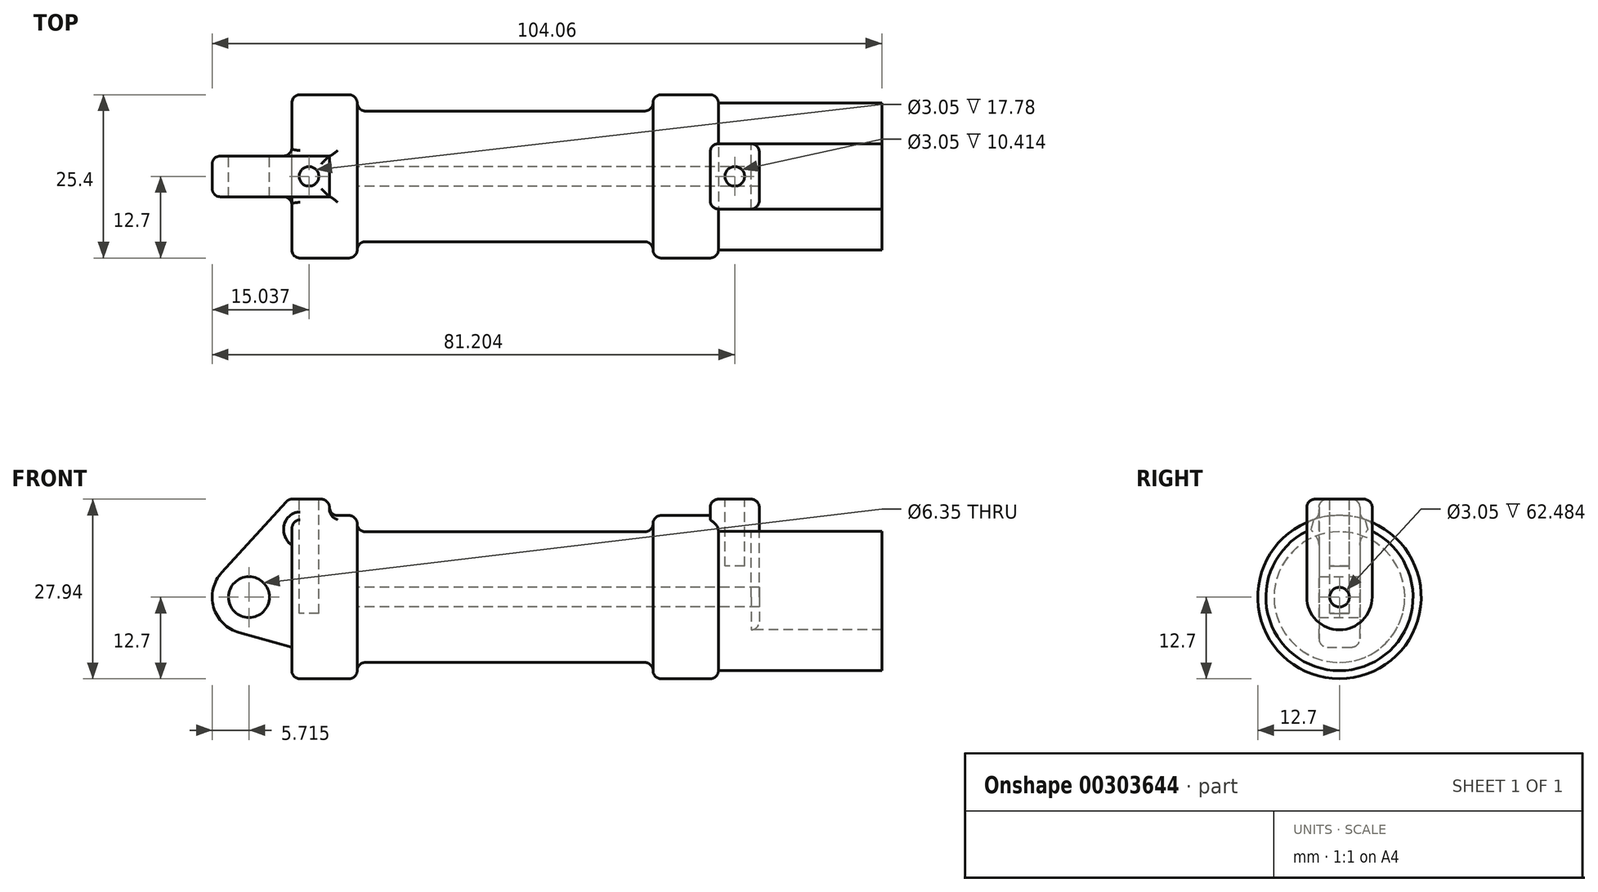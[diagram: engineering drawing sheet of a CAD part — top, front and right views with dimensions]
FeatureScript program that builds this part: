
annotation { "Feature Type Name" : "Feature", "Feature Type Description" : "" }
export const myFeature = defineFeature(function(context is Context, id is Id, definition is map)
    precondition{}
    {
        {
            var Q0;
            Q0=qCreatedBy(makeId("Front.planeOp"),FACE);
            var sketch = newSketch(context, id + "F0", { "sketchPlane" : qUnion([Q0])});
            skLineSegment(sketch, "E0", {"start": v(0, 0) * mm, "end": v(0, 12.7) * mm});
            skLineSegment(sketch, "E1", {"start": v(0, 12.7) * mm, "end": v(10.16, 12.7) * mm});
            skLineSegment(sketch, "E2", {"start": v(10.16, 12.7) * mm, "end": v(10.16, 10.16) * mm});
            skLineSegment(sketch, "E3", {"start": v(10.16, 10.16) * mm, "end": v(56.13, 10.16) * mm});
            skLineSegment(sketch, "E4", {"start": v(56.13, 10.16) * mm, "end": v(56.13, 12.7) * mm});
            skLineSegment(sketch, "E5", {"start": v(56.13, 12.7) * mm, "end": v(66.3, 12.7) * mm});
            skLineSegment(sketch, "E6", {"start": v(66.3, 12.7) * mm, "end": v(66.3, 0) * mm});
            skLineSegment(sketch, "E7", {"start": v(66.3, 0) * mm, "end": v(0, 0) * mm});
            skLineSegment(sketch, "E8", {"start": v(5.84, 15.24) * mm, "end": v(-0.5, 15.24) * mm});
            skLineSegment(sketch, "E9", {"start": v(-0.5, 15.24) * mm, "end": v(-10.88, 3.85) * mm});
            skLineSegment(sketch, "E10", {"start": v(0, 0) * mm, "end": v(-6.65, 0) * mm});
            skCircle(sketch, "E11", {"center": v(-6.65, 0) * mm, "radius": 5.72 * mm});
            skCircle(sketch, "E12", {"center": v(-6.65, 0) * mm, "radius": 3.18 * mm});
            skLineSegment(sketch, "E13", {"start": v(5.84, 15.24) * mm, "end": v(5.84, -9.4) * mm});
            skLineSegment(sketch, "E14", {"start": v(5.84, -9.4) * mm, "end": v(-8.18, -5.5) * mm});
            skSolve(sketch);
        }
        {
            var Q0;
            {var subQ0=sQuery(id+"F0.wireOp",EDGE,"E2");Q0=makeQuery(id+"F0.imprint","IMPRINT",FACE,{"disambiguationData":[TD([[makeQuery(id+"F0.imprint","IMPRINT",EDGE,{"derivedFrom":subQ0}),-1.0]])]});}
            var Q1;
            {var subQ0=sQuery(id+"F0.wireOp",EDGE,"E0");Q1=makeQuery(id+"F0.imprint","IMPRINT",FACE,{"disambiguationData":[TD([[makeQuery(id+"F0.imprint","IMPRINT",EDGE,{"derivedFrom":subQ0}),-1.0]])]});}
            var Q2;
            Q2=sQuery(id+"F0.wireOp",EDGE,"E7");
            revolve(context, id + "F1", {"entities" : qUnion([Q0, Q1]), "axis" : qUnion([Q2]), "revolveType" : RevolveType.FULL});
        }
        {
            var Q0;
            {var subQ1=sQuery(id+"F0.wireOp",EDGE,"E0");Q0=makeQuery(id+"F0.imprint","IMPRINT",FACE,{"disambiguationData":[TD([[makeQuery(id+"F0.imprint","IMPRINT",EDGE,{"derivedFrom":subQ1}),1.0]])]});}
            var Q1;
            {var subQ5=sQuery(id+"F0.wireOp",EDGE,"E12");Q1=makeQuery(id+"F0.imprint","IMPRINT",FACE,{"disambiguationData":[TD([[makeQuery(id+"F0.imprint","IMPRINT",EDGE,{"derivedFrom":subQ5}),-1.0]])]});}
            var Q2;
            {var subQ0=sQuery(id+"F0.wireOp",EDGE,"E14");Q2=makeQuery(id+"F0.imprint","IMPRINT",FACE,{"disambiguationData":[TD([[makeQuery(id+"F0.imprint","IMPRINT",EDGE,{"derivedFrom":subQ0}),-1.0]])]});}
            var Q3;
            {var subQ0=sQuery(id+"F0.wireOp",EDGE,"E0");Q3=makeQuery(id+"F0.imprint","IMPRINT",FACE,{"disambiguationData":[TD([[makeQuery(id+"F0.imprint","IMPRINT",EDGE,{"derivedFrom":subQ0}),-1.0]])]});}
            extrude(context, id + "F2", {"entities" : qUnion([Q0, Q1, Q2, Q3]), "operationType" : NewBodyOperationType.ADD, "depth" : 6.35 * mm, "symmetric" : true});
        }
        {
            var Q0;
            Q0=makeQuery(id+"F1.opRevolve","SWEPT_FACE",FACE,{"disambiguationData":[OSD([sQuery(id+"F0.wireOp",EDGE,"E6")])]});
            var sketch = newSketch(context, id + "F3", { "sketchPlane" : qUnion([Q0])});
            skCircle(sketch, "E15", {"center": v(0, 0) * mm, "radius": 1.52 * mm});
            skCircle(sketch, "E16", {"center": v(0, 0) * mm, "radius": 5.08 * mm});
            skLineSegment(sketch, "E17", {"start": v(-5.08, 0) * mm, "end": v(-5.08, 15.24) * mm});
            skLineSegment(sketch, "E18", {"start": v(5.08, 0) * mm, "end": v(5.08, 15.24) * mm});
            skLineSegment(sketch, "E19", {"start": v(-5.08, 15.24) * mm, "end": v(5.08, 15.24) * mm});
            skSolve(sketch);
        }
        {
            var Q0;
            {var subQ0=sQuery(id+"F3.wireOp",EDGE,"E19");Q0=makeQuery(id+"F3.imprint","IMPRINT",FACE,{"disambiguationData":[TD([[makeQuery(id+"F3.imprint","IMPRINT",EDGE,{"derivedFrom":subQ0}),-1.0]])]});}
            var Q1;
            {var subQ0=sQuery(id+"F3.wireOp",EDGE,"E17");var subQ1=sQuery(id+"F3.wireOp",EDGE,"E16");var subQ2=makeQuery(id+"F3.imprint","INTERSECT",VERTEX,{"derivedFrom":[subQ1,subQ0]});Q1=makeQuery(id+"F3.imprint","IMPRINT",FACE,{"disambiguationData":[TD([[makeQuery(id+"F3.imprint","IMPRINT",EDGE,{"disambiguationData":[TD([[subQ2,1.0]])],"derivedFrom":subQ1}),-1.0]])]});}
            var Q2;
            Q2=makeQuery(id+"F3.imprint","IMPRINT",FACE,{"disambiguationData":[TD([[makeQuery(id+"F3.imprint","IMPRINT",EDGE,{"derivedFrom":sQuery(id+"F3.wireOp",EDGE,"E15")}),-1.0]])]});
            extrude(context, id + "F4", {"entities" : qUnion([Q0, Q1, Q2]), "operationType" : NewBodyOperationType.ADD, "depth" : 6.35 * mm, "hasSecondDirection" : true, "secondDirectionOppositeDirection" : true, "secondDirectionDepth" : 1.27 * mm});
        }
        {
            var Q0;
            Q0=makeQuery(id+"F4.boolean.opBoolean","SPLIT",FACE,{"disambiguationData":[TD([makeQuery(id+"F4.opExtrude","SWEPT_FACE",FACE,{"disambiguationData":[OSD([sQuery(id+"F3.wireOp",EDGE,"E15")])]})])],"derivedFrom":makeQuery(id+"F1.opRevolve","SWEPT_FACE",FACE,{"disambiguationData":[OSD([sQuery(id+"F0.wireOp",EDGE,"E6")])]})});
            var Q1;
            Q1=makeQuery(id+"F1.opRevolve","SWEPT_FACE",FACE,{"disambiguationData":[OSD([sQuery(id+"F0.wireOp",EDGE,"E2")])]});
            extrude(context, id + "F5", {"entities" : qUnion([Q0]), "operationType" : NewBodyOperationType.REMOVE, "endBound" : BoundingType.UP_TO_SURFACE, "oppositeDirection" : true, "endBoundEntityFace" : qUnion([Q1]), "depth" : 25.4 * mm});
        }
        {
            var Q0;
            Q0=makeQuery(id+"F2.opExtrude","SWEPT_FACE",FACE,{"disambiguationData":[OSD([sQuery(id+"F0.wireOp",EDGE,"E8")])]});
            var sketch = newSketch(context, id + "F6", { "sketchPlane" : qUnion([Q0])});
            skCircle(sketch, "E20", {"center": v(2.67, 0) * mm, "radius": 1.52 * mm});
            skSolve(sketch);
        }
        {
            var Q0;
            Q0=makeQuery(id+"F4.opExtrude","SWEPT_FACE",FACE,{"disambiguationData":[OSD([sQuery(id+"F3.wireOp",EDGE,"E19")])]});
            var sketch = newSketch(context, id + "F7", { "sketchPlane" : qUnion([Q0])});
            skCircle(sketch, "E21", {"center": v(68.83, 0) * mm, "radius": 1.52 * mm});
            skSolve(sketch);
        }
        {
            var Q0;
            Q0=makeQuery(id+"F6.imprint","IMPRINT",FACE,{"disambiguationData":[TD([[makeQuery(id+"F6.imprint","IMPRINT",EDGE,{"derivedFrom":sQuery(id+"F6.wireOp",EDGE,"E20")}),1.0]])]});
            extrude(context, id + "F8", {"entities" : qUnion([Q0]), "operationType" : NewBodyOperationType.REMOVE, "oppositeDirection" : true, "depth" : 17.78 * mm});
        }
        {
            var Q0;
            Q0=makeQuery(id+"F7.imprint","IMPRINT",FACE,{"disambiguationData":[TD([[makeQuery(id+"F7.imprint","IMPRINT",EDGE,{"derivedFrom":sQuery(id+"F7.wireOp",EDGE,"E21")}),1.0]])]});
            extrude(context, id + "F9", {"entities" : qUnion([Q0]), "operationType" : NewBodyOperationType.REMOVE, "oppositeDirection" : true, "depth" : 10.4 * mm});
        }
        {
            var Q0;
            Q0=makeQuery(id+"F1.opRevolve","SWEPT_EDGE",EDGE,{"disambiguationData":[OSD([sQuery(id+"F0.wireOp",EDGE,"E5"),sQuery(id+"F0.wireOp",EDGE,"E6")])]});
            var Q1;
            Q1=makeQuery(id+"F1.opRevolve","SWEPT_EDGE",EDGE,{"disambiguationData":[OSD([sQuery(id+"F0.wireOp",EDGE,"E4"),sQuery(id+"F0.wireOp",EDGE,"E5")])]});
            var Q2;
            Q2=makeQuery(id+"F1.opRevolve","SWEPT_FACE",FACE,{"disambiguationData":[OSD([sQuery(id+"F0.wireOp",EDGE,"E3")])]});
            var Q3;
            Q3=makeQuery(id+"F1.opRevolve","SWEPT_FACE",FACE,{"disambiguationData":[OSD([sQuery(id+"F0.wireOp",EDGE,"E1")])]});
            var Q4;
            Q4=makeQuery(id+"F1.opRevolve","SWEPT_EDGE",EDGE,{"disambiguationData":[OSD([sQuery(id+"F0.wireOp",EDGE,"E0"),sQuery(id+"F0.wireOp",EDGE,"E1")])]});
            fillet(context, id + "F10", {"entities" : qUnion([Q0, Q1, Q2, Q3, Q4]), "radius" : 1.27 * mm, "tangentPropagation" : true, "allowEdgeOverflow" : false});
        }
        {
            var Q0;
            Q0=makeQuery(id+"F2.opExtrude","SWEPT_FACE",FACE,{"disambiguationData":[OSD([sQuery(id+"F0.wireOp",EDGE,"E9")])]});
            var Q1;
            Q1=makeQuery(id+"F2.opExtrude","CAP_EDGE",EDGE,{"disambiguationData":[OSD([sQuery(id+"F0.wireOp",EDGE,"E8")])],"isStart":true});
            var Q2;
            Q2=makeQuery(id+"F2.opExtrude","SWEPT_EDGE",EDGE,{"disambiguationData":[OSD([sQuery(id+"F0.wireOp",EDGE,"E8"),sQuery(id+"F0.wireOp",EDGE,"E13")])]});
            var Q3;
            Q3=makeQuery(id+"F2.opExtrude","CAP_EDGE",EDGE,{"disambiguationData":[OSD([sQuery(id+"F0.wireOp",EDGE,"E8")])],"isStart":false});
            fillet(context, id + "F11", {"entities" : qUnion([Q0, Q1, Q2, Q3]), "radius" : 1.27 * mm, "tangentPropagation" : true, "allowEdgeOverflow" : false});
        }
        {
            var Q0;
            Q0=makeQuery(id+"F4.opExtrude","CAP_EDGE",EDGE,{"disambiguationData":[OSD([sQuery(id+"F3.wireOp",EDGE,"E18")])],"isStart":false});
            var Q1;
            Q1=makeQuery(id+"F4.opExtrude","CAP_EDGE",EDGE,{"disambiguationData":[OSD([sQuery(id+"F3.wireOp",EDGE,"E19")])],"isStart":false});
            var Q2;
            Q2=makeQuery(id+"F4.opExtrude","SWEPT_EDGE",EDGE,{"disambiguationData":[OSD([sQuery(id+"F3.wireOp",EDGE,"E17"),sQuery(id+"F3.wireOp",EDGE,"E19")])]});
            var Q3;
            Q3=makeQuery(id+"F4.opExtrude","CAP_EDGE",EDGE,{"disambiguationData":[OSD([sQuery(id+"F3.wireOp",EDGE,"E19")])],"isStart":true});
            var Q4;
            Q4=makeQuery(id+"F4.opExtrude","SWEPT_EDGE",EDGE,{"disambiguationData":[OSD([sQuery(id+"F3.wireOp",EDGE,"E18"),sQuery(id+"F3.wireOp",EDGE,"E19")])]});
            var Q5;
            Q5=makeQuery(id+"F4.opExtrude","CAP_EDGE",EDGE,{"disambiguationData":[OSD([sQuery(id+"F3.wireOp",EDGE,"E18")])],"isStart":true});
            var Q6;
            Q6=makeQuery(id+"F4.opExtrude","CAP_EDGE",EDGE,{"disambiguationData":[OSD([sQuery(id+"F3.wireOp",EDGE,"E17")])],"isStart":true});
            fillet(context, id + "F12", {"entities" : qUnion([Q0, Q1, Q2, Q3, Q4, Q5, Q6]), "radius" : 1.27 * mm, "tangentPropagation" : true, "allowEdgeOverflow" : false});
        }
        {
            var Q0;
            {var subQ0=sQuery(id+"FXvLCQylG0OJOqs_1.wireOp",EDGE,"3RpC5Bgf-b7m6-Ug9A-TNXq-2KlfdZ5rkiCp");Q0=makeQuery(id+"FXvLCQylG0OJOqs_1.imprint","IMPRINT",FACE,{"disambiguationData":[TD([[makeQuery(id+"FXvLCQylG0OJOqs_1.imprint","IMPRINT",EDGE,{"derivedFrom":subQ0}),-1.0]])]});}
            var Q1;
            Q1=makeQuery(id+"F1.opRevolve","SWEPT_FACE",FACE,{"disambiguationData":[OSD([sQuery(id+"F0.wireOp",EDGE,"E6")])]});
            extrude(context, id + "F13", {"entities" : qUnion([Q0, Q1]), "operationType" : NewBodyOperationType.ADD, "depth" : 25.4 * mm});
        }
    });
